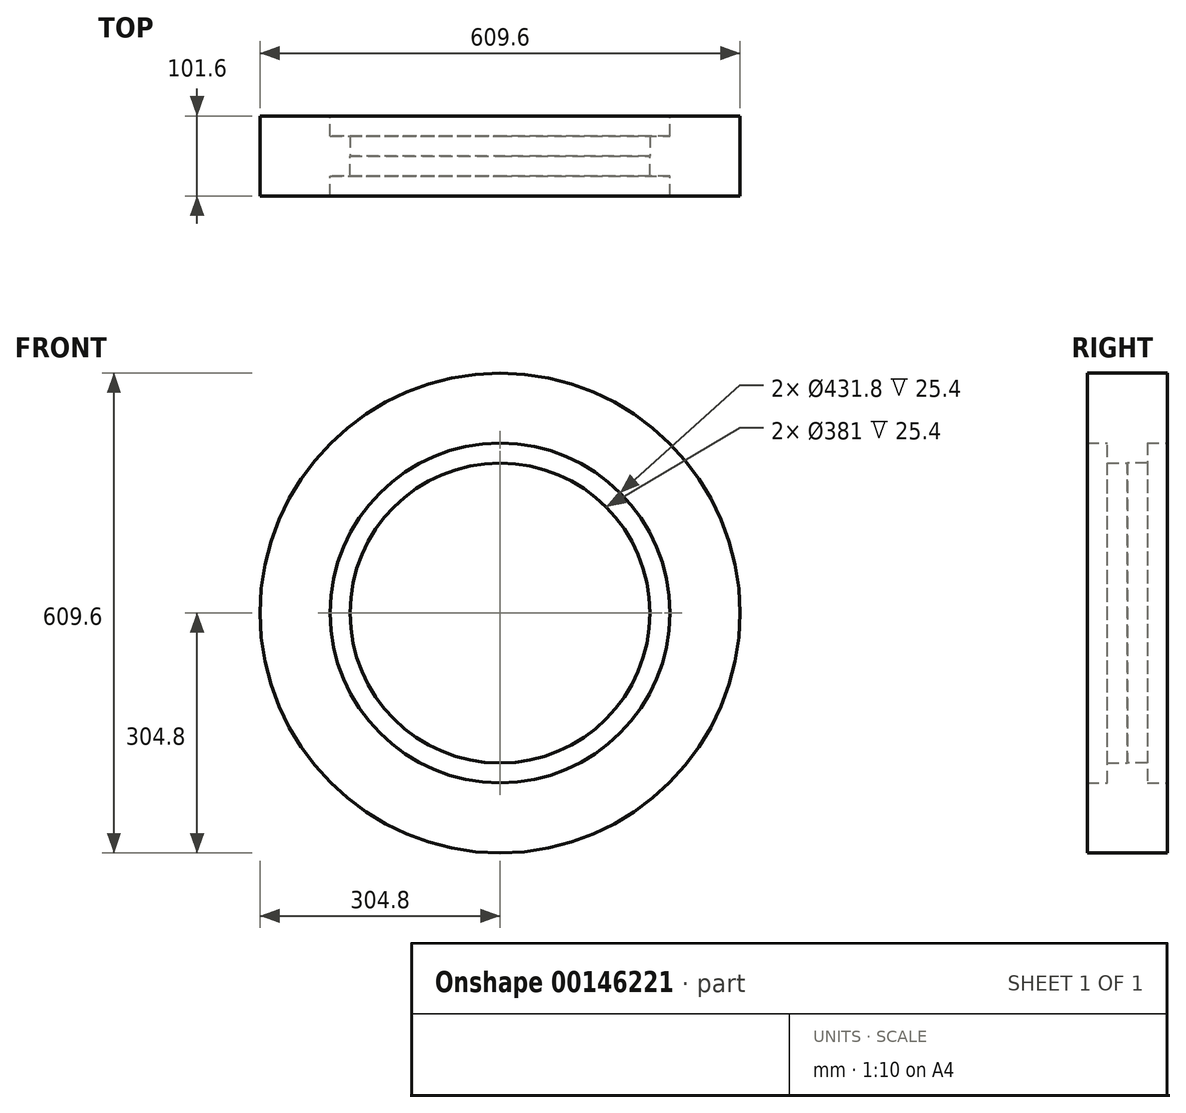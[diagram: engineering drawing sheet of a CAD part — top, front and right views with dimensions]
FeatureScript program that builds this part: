
annotation { "Feature Type Name" : "Feature", "Feature Type Description" : "" }
export const myFeature = defineFeature(function(context is Context, id is Id, definition is map)
    precondition{}
    {
        {
            var Q0;
            Q0=qCreatedBy(makeId("Front.planeOp"),FACE);
            var sketch = newSketch(context, id + "F0", { "sketchPlane" : qUnion([Q0])});
            skCircle(sketch, "E0", {"center": v(0, 0) * mm, "radius": 215.9 * mm});
            skCircle(sketch, "E1", {"center": v(0, 0) * mm, "radius": 304.8 * mm});
            skSolve(sketch);
        }
        {
            var Q0;
            Q0=makeQuery(id+"F0.imprint","IMPRINT",FACE,{"disambiguationData":[TD([[makeQuery(id+"F0.imprint","IMPRINT",EDGE,{"derivedFrom":sQuery(id+"F0.wireOp",EDGE,"E0")}),-1.0]])]});
            extrude(context, id + "F1", {"entities" : qUnion([Q0]), "depth" : 101.6 * mm});
        }
        {
            var Q0;
            Q0=makeQuery(id+"F1.opExtrude","CAP_FACE",FACE,{"disambiguationData":[OSD([sQuery(id+"F0.wireOp",EDGE,"E0"),sQuery(id+"F0.wireOp",EDGE,"E1")])],"isStart":false});
            cPlane(context, id + "F2", {"entities" : qUnion([Q0]), "cplaneType" : CPlaneType.OFFSET, "offset" : 50.8 * mm, "oppositeDirection" : true, "width" : 152.4 * mm, "height" : 152.4 * mm});
        }
        {
            var Q0;
            Q0=qCreatedBy(id+"F2.planeOp",FACE);
            var sketch = newSketch(context, id + "F3", { "sketchPlane" : qUnion([Q0])});
            skCircle(sketch, "E2", {"center": v(0, 0) * mm, "radius": 224.34 * mm});
            skCircle(sketch, "E3", {"center": v(0, 0) * mm, "radius": 190.5 * mm});
            skSolve(sketch);
        }
        {
            var Q0;
            Q0=makeQuery(id+"F3.imprint","IMPRINT",FACE,{"disambiguationData":[TD([[makeQuery(id+"F3.imprint","IMPRINT",EDGE,{"derivedFrom":sQuery(id+"F3.wireOp",EDGE,"E2")}),1.0]])]});
            extrude(context, id + "F4", {"entities" : qUnion([Q0]), "operationType" : NewBodyOperationType.ADD, "depth" : 25.4 * mm});
        }
        {
            var Q0;
            Q0=makeQuery(id+"F4.opExtrude","CAP_FACE",FACE,{"disambiguationData":[OSD([sQuery(id+"F3.wireOp",EDGE,"E2"),sQuery(id+"F3.wireOp",EDGE,"E3")])],"isStart":true});
            var sketch = newSketch(context, id + "F5", { "sketchPlane" : qUnion([Q0])});
            skCircle(sketch, "E4", {"center": v(0, 0) * mm, "radius": 190.5 * mm});
            skCircle(sketch, "E5", {"center": v(0, 0) * mm, "radius": 221.57 * mm});
            skSolve(sketch);
        }
        {
            var Q0;
            Q0=makeQuery(id+"F5.imprint","IMPRINT",FACE,{"disambiguationData":[TD([[makeQuery(id+"F5.imprint","IMPRINT",EDGE,{"derivedFrom":sQuery(id+"F5.wireOp",EDGE,"E4")}),-1.0]])]});
            extrude(context, id + "F6", {"entities" : qUnion([Q0]), "operationType" : NewBodyOperationType.ADD, "depth" : 25.4 * mm});
        }
    });
